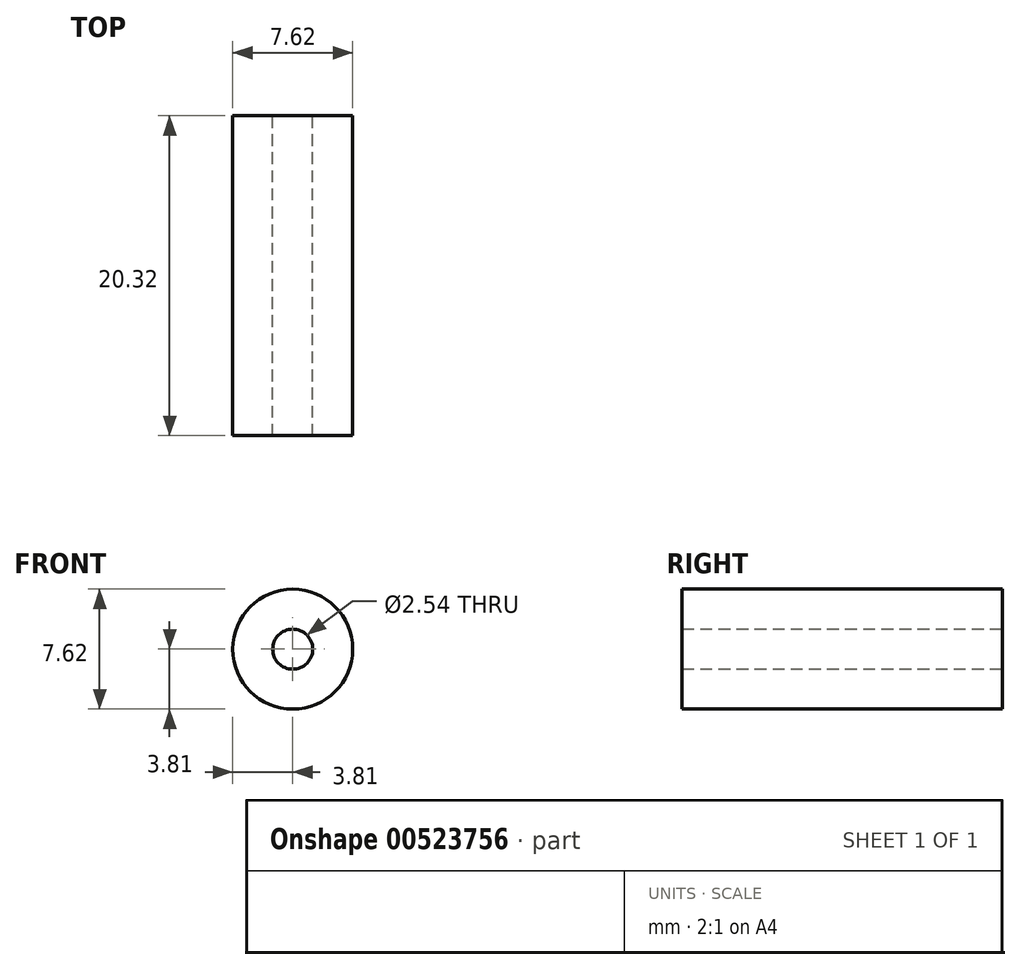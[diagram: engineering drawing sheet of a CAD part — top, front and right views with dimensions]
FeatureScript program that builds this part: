
annotation { "Feature Type Name" : "Feature", "Feature Type Description" : "" }
export const myFeature = defineFeature(function(context is Context, id is Id, definition is map)
    precondition{}
    {
        {
            var Q0;
            Q0=qCreatedBy(makeId("Front.planeOp"),FACE);
            var sketch = newSketch(context, id + "F0", { "sketchPlane" : qUnion([Q0])});
            skCircle(sketch, "E0", {"center": v(0, 0) * mm, "radius": 3.81 * mm});
            skCircle(sketch, "E1", {"center": v(0, 0) * mm, "radius": 1.27 * mm});
            skSolve(sketch);
        }
        {
            var Q0;
            Q0 = qSketchRegion(id + "F0", true);
            extrude(context, id + "F1", {"entities" : qUnion([Q0]), "depth" : 19.05 * mm, "offsetDistance" : 25.4 * mm});
        }
        {
            var Q0;
            Q0=makeQuery(id+"F1.opExtrude","CAP_FACE",FACE,{"disambiguationData":[OSD([sQuery(id+"F0.wireOp",EDGE,"E0"),sQuery(id+"F0.wireOp",EDGE,"E1")])],"isStart":false});
            extrude(context, id + "F2", {"entities" : qUnion([Q0]), "operationType" : NewBodyOperationType.ADD, "depth" : 6.35 * mm, "offsetDistance" : 25.4 * mm});
        }
        {
            var Q0;
            Q0=makeQuery(id+"F2.opExtrude","CAP_FACE",FACE,{"disambiguationData":[OSD([sQuery(id+"F0.wireOp",EDGE,"E0"),sQuery(id+"F0.wireOp",EDGE,"E1")])],"isStart":false});
            extrude(context, id + "F3", {"entities" : qUnion([Q0]), "operationType" : NewBodyOperationType.REMOVE, "oppositeDirection" : true, "depth" : 5.08 * mm, "offsetDistance" : 25.4 * mm});
        }
    });
